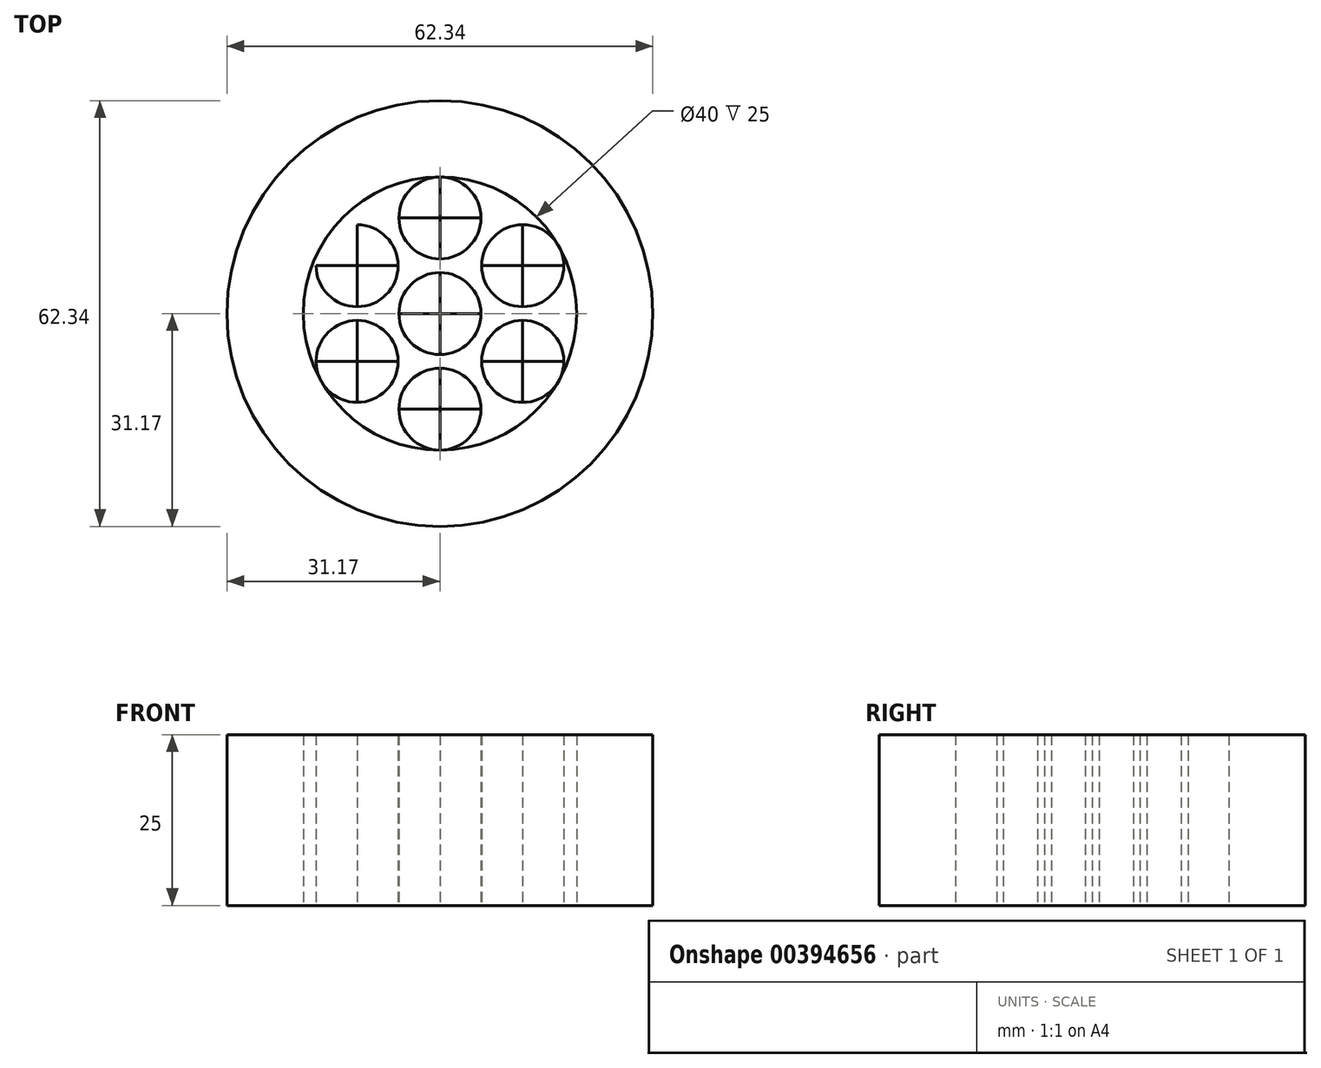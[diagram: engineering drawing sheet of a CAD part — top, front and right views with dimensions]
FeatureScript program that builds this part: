
annotation { "Feature Type Name" : "Feature", "Feature Type Description" : "" }
export const myFeature = defineFeature(function(context is Context, id is Id, definition is map)
    precondition{}
    {
        {
            var Q0;
            Q0=qCreatedBy(makeId("Top.planeOp"),FACE);
            var sketch = newSketch(context, id + "F0", { "sketchPlane" : qUnion([Q0])});
            skCircle(sketch, "E0", {"center": v(0, 0) * mm, "radius": 20 * mm});
            skCircle(sketch, "E1", {"center": v(0, 14) * mm, "radius": 6 * mm});
            skCircle(sketch, "E2.1.0", {"center": v(-12.12, 7) * mm, "radius": 6 * mm});
            skCircle(sketch, "E2.2.0", {"center": v(-12.12, -7) * mm, "radius": 6 * mm});
            skCircle(sketch, "E3.1.3.0", {"center": v(0, -14) * mm, "radius": 6 * mm});
            skCircle(sketch, "E3.1.4.0", {"center": v(12.12, -7) * mm, "radius": 6 * mm});
            skCircle(sketch, "E3.1.5.0", {"center": v(12.12, 7) * mm, "radius": 6 * mm});
            skCircle(sketch, "E4", {"center": v(0, 0) * mm, "radius": 6 * mm});
            skLineSegment(sketch, "E5", {"start": v(-18.12, 7) * mm, "end": v(-6.12, 7) * mm});
            skLineSegment(sketch, "E6", {"start": v(-18.12, -7) * mm, "end": v(-6.12, -7) * mm});
            skLineSegment(sketch, "E7", {"start": v(12.12, -13) * mm, "end": v(12.12, 13) * mm});
            skLineSegment(sketch, "E8", {"start": v(-12.12, -13) * mm, "end": v(-12.12, 13) * mm});
            skLineSegment(sketch, "E9", {"start": v(0, 14) * mm, "end": v(0, 20) * mm});
            skLineSegment(sketch, "E10", {"start": v(0, 14) * mm, "end": v(0, 8) * mm});
            skLineSegment(sketch, "E11", {"start": v(0, 0) * mm, "end": v(-6, 0) * mm});
            skLineSegment(sketch, "E12", {"start": v(0, 0) * mm, "end": v(6, 0) * mm});
            skLineSegment(sketch, "E13", {"start": v(0, 14) * mm, "end": v(-6, 14) * mm});
            skLineSegment(sketch, "E14", {"start": v(0, 14) * mm, "end": v(6, 14) * mm});
            skLineSegment(sketch, "E15", {"start": v(0, -14) * mm, "end": v(-6, -14) * mm});
            skLineSegment(sketch, "E16", {"start": v(0, -14) * mm, "end": v(6, -14) * mm});
            skLineSegment(sketch, "E17.trimOffspring", {"start": v(6.12, -7) * mm, "end": v(18.12, -7) * mm});
            skLineSegment(sketch, "E18.trimOffspring", {"start": v(0, -8) * mm, "end": v(0, -20) * mm});
            skLineSegment(sketch, "E19.trimOffspring", {"start": v(6.12, 7) * mm, "end": v(18.12, 7) * mm});
            skLineSegment(sketch, "E20.trimOffspring", {"start": v(0, 6) * mm, "end": v(0, -6) * mm});
            skCircle(sketch, "E21", {"center": v(0, 0) * mm, "radius": 31.17 * mm});
            skSolve(sketch);
        }
        {
            var Q0;
            {var subQ0=sQuery(id+"F0.wireOp",EDGE,"E16");Q0=makeQuery(id+"F0.imprint","IMPRINT",FACE,{"disambiguationData":[TD([[makeQuery(id+"F0.imprint","IMPRINT",EDGE,{"derivedFrom":subQ0}),-1.0]])]});}
            var Q1;
            {var subQ0=sQuery(id+"F0.wireOp",EDGE,"E15");Q1=makeQuery(id+"F0.imprint","IMPRINT",FACE,{"disambiguationData":[TD([[makeQuery(id+"F0.imprint","IMPRINT",EDGE,{"derivedFrom":subQ0}),-1.0]])]});}
            var Q2;
            {var subQ0=sQuery(id+"F0.wireOp",EDGE,"E8");var subQ1=sQuery(id+"F0.wireOp",EDGE,"E2.1.0");var subQ2=makeQuery(id+"F0.imprint","INTERSECT",VERTEX,{"disambiguationData":[OD(0.0)],"derivedFrom":[subQ1,subQ0]});Q2=makeQuery(id+"F0.imprint","IMPRINT",FACE,{"disambiguationData":[TD([[makeQuery(id+"F0.imprint","IMPRINT",EDGE,{"disambiguationData":[TD([[subQ2,-1.0]])],"derivedFrom":subQ1}),1.0]])]});}
            var Q3;
            {var subQ0=sQuery(id+"F0.wireOp",EDGE,"E11");Q3=makeQuery(id+"F0.imprint","IMPRINT",FACE,{"disambiguationData":[TD([[makeQuery(id+"F0.imprint","IMPRINT",EDGE,{"derivedFrom":subQ0}),-1.0]])]});}
            var Q4;
            {var subQ0=sQuery(id+"F0.wireOp",EDGE,"E12");Q4=makeQuery(id+"F0.imprint","IMPRINT",FACE,{"disambiguationData":[TD([[makeQuery(id+"F0.imprint","IMPRINT",EDGE,{"derivedFrom":subQ0}),-1.0]])]});}
            var Q5;
            {var subQ0=sQuery(id+"F0.wireOp",EDGE,"E9");Q5=makeQuery(id+"F0.imprint","IMPRINT",FACE,{"disambiguationData":[TD([[makeQuery(id+"F0.imprint","IMPRINT",EDGE,{"derivedFrom":subQ0}),1.0]])]});}
            var Q6;
            {var subQ0=sQuery(id+"F0.wireOp",EDGE,"E10");Q6=makeQuery(id+"F0.imprint","IMPRINT",FACE,{"disambiguationData":[TD([[makeQuery(id+"F0.imprint","IMPRINT",EDGE,{"derivedFrom":subQ0}),1.0]])]});}
            var Q7;
            {var subQ0=sQuery(id+"F0.wireOp",EDGE,"E5");var subQ1=sQuery(id+"F0.wireOp",EDGE,"E2.1.0");var subQ2=makeQuery(id+"F0.imprint","INTERSECT",VERTEX,{"disambiguationData":[OD(1.0)],"derivedFrom":[subQ1,subQ0]});Q7=makeQuery(id+"F0.imprint","IMPRINT",FACE,{"disambiguationData":[TD([[makeQuery(id+"F0.imprint","IMPRINT",EDGE,{"disambiguationData":[TD([[subQ2,1.0]])],"derivedFrom":subQ1}),1.0]])]});}
            var Q8;
            {var subQ0=sQuery(id+"F0.wireOp",EDGE,"E6");var subQ1=sQuery(id+"F0.wireOp",EDGE,"E2.2.0");var subQ2=makeQuery(id+"F0.imprint","INTERSECT",VERTEX,{"disambiguationData":[OD(0.0)],"derivedFrom":[subQ1,subQ0]});Q8=makeQuery(id+"F0.imprint","IMPRINT",FACE,{"disambiguationData":[TD([[makeQuery(id+"F0.imprint","IMPRINT",EDGE,{"disambiguationData":[TD([[subQ2,1.0]])],"derivedFrom":subQ1}),1.0]])]});}
            var Q9;
            {var subQ0=sQuery(id+"F0.wireOp",EDGE,"E6");var subQ1=sQuery(id+"F0.wireOp",EDGE,"E2.2.0");var subQ2=makeQuery(id+"F0.imprint","INTERSECT",VERTEX,{"disambiguationData":[OD(1.0)],"derivedFrom":[subQ1,subQ0]});Q9=makeQuery(id+"F0.imprint","IMPRINT",FACE,{"disambiguationData":[TD([[makeQuery(id+"F0.imprint","IMPRINT",EDGE,{"disambiguationData":[TD([[subQ2,1.0]])],"derivedFrom":subQ1}),1.0]])]});}
            var Q10;
            {var subQ0=sQuery(id+"F0.wireOp",EDGE,"E19.trimOffspring");var subQ1=sQuery(id+"F0.wireOp",EDGE,"E3.1.5.0");var subQ2=makeQuery(id+"F0.imprint","INTERSECT",VERTEX,{"disambiguationData":[OD(1.0)],"derivedFrom":[subQ1,subQ0]});Q10=makeQuery(id+"F0.imprint","IMPRINT",FACE,{"disambiguationData":[TD([[makeQuery(id+"F0.imprint","IMPRINT",EDGE,{"disambiguationData":[TD([[subQ2,1.0]])],"derivedFrom":subQ1}),1.0]])]});}
            var Q11;
            {var subQ0=sQuery(id+"F0.wireOp",EDGE,"E17.trimOffspring");var subQ1=sQuery(id+"F0.wireOp",EDGE,"E3.1.4.0");var subQ2=makeQuery(id+"F0.imprint","INTERSECT",VERTEX,{"disambiguationData":[OD(0.0)],"derivedFrom":[subQ1,subQ0]});Q11=makeQuery(id+"F0.imprint","IMPRINT",FACE,{"disambiguationData":[TD([[makeQuery(id+"F0.imprint","IMPRINT",EDGE,{"disambiguationData":[TD([[subQ2,1.0]])],"derivedFrom":subQ1}),1.0]])]});}
            var Q12;
            {var subQ0=sQuery(id+"F0.wireOp",EDGE,"E7");var subQ1=sQuery(id+"F0.wireOp",EDGE,"E3.1.4.0");var subQ2=makeQuery(id+"F0.imprint","INTERSECT",VERTEX,{"disambiguationData":[OD(0.0)],"derivedFrom":[subQ1,subQ0]});Q12=makeQuery(id+"F0.imprint","IMPRINT",FACE,{"disambiguationData":[TD([[makeQuery(id+"F0.imprint","IMPRINT",EDGE,{"disambiguationData":[TD([[subQ2,-1.0]])],"derivedFrom":subQ1}),1.0]])]});}
            var Q13;
            {var subQ0=sQuery(id+"F0.wireOp",EDGE,"E7");var subQ1=sQuery(id+"F0.wireOp",EDGE,"E3.1.5.0");var subQ2=makeQuery(id+"F0.imprint","INTERSECT",VERTEX,{"disambiguationData":[OD(0.0)],"derivedFrom":[subQ1,subQ0]});Q13=makeQuery(id+"F0.imprint","IMPRINT",FACE,{"disambiguationData":[TD([[makeQuery(id+"F0.imprint","IMPRINT",EDGE,{"disambiguationData":[TD([[subQ2,-1.0]])],"derivedFrom":subQ1}),1.0]])]});}
            extrude(context, id + "F1", {"entities" : qUnion([Q0, Q1, Q2, Q3, Q4, Q5, Q6, Q7, Q8, Q9, Q10, Q11, Q12, Q13]), "depth" : 25 * mm});
        }
        {
            var Q0;
            {var subQ0=sQuery(id+"F0.wireOp",EDGE,"E5");var subQ1=sQuery(id+"F0.wireOp",EDGE,"E2.1.0");var subQ2=makeQuery(id+"F0.imprint","INTERSECT",VERTEX,{"disambiguationData":[OD(1.0)],"derivedFrom":[subQ1,subQ0]});Q0=makeQuery(id+"F0.imprint","IMPRINT",FACE,{"disambiguationData":[TD([[makeQuery(id+"F0.imprint","IMPRINT",EDGE,{"disambiguationData":[TD([[subQ2,-1.0]])],"derivedFrom":subQ1}),1.0]])]});}
            var Q1;
            {var subQ0=sQuery(id+"F0.wireOp",EDGE,"E5");var subQ1=sQuery(id+"F0.wireOp",EDGE,"E2.1.0");var subQ2=makeQuery(id+"F0.imprint","INTERSECT",VERTEX,{"disambiguationData":[OD(0.0)],"derivedFrom":[subQ1,subQ0]});Q1=makeQuery(id+"F0.imprint","IMPRINT",FACE,{"disambiguationData":[TD([[makeQuery(id+"F0.imprint","IMPRINT",EDGE,{"disambiguationData":[TD([[subQ2,-1.0]])],"derivedFrom":subQ1}),1.0]])]});}
            var Q2;
            {var subQ0=sQuery(id+"F0.wireOp",EDGE,"E9");Q2=makeQuery(id+"F0.imprint","IMPRINT",FACE,{"disambiguationData":[TD([[makeQuery(id+"F0.imprint","IMPRINT",EDGE,{"derivedFrom":subQ0}),-1.0]])]});}
            var Q3;
            {var subQ0=sQuery(id+"F0.wireOp",EDGE,"E10");Q3=makeQuery(id+"F0.imprint","IMPRINT",FACE,{"disambiguationData":[TD([[makeQuery(id+"F0.imprint","IMPRINT",EDGE,{"derivedFrom":subQ0}),-1.0]])]});}
            var Q4;
            {var subQ0=sQuery(id+"F0.wireOp",EDGE,"E12");Q4=makeQuery(id+"F0.imprint","IMPRINT",FACE,{"disambiguationData":[TD([[makeQuery(id+"F0.imprint","IMPRINT",EDGE,{"derivedFrom":subQ0}),1.0]])]});}
            var Q5;
            {var subQ0=sQuery(id+"F0.wireOp",EDGE,"E11");Q5=makeQuery(id+"F0.imprint","IMPRINT",FACE,{"disambiguationData":[TD([[makeQuery(id+"F0.imprint","IMPRINT",EDGE,{"derivedFrom":subQ0}),1.0]])]});}
            var Q6;
            {var subQ0=sQuery(id+"F0.wireOp",EDGE,"E19.trimOffspring");var subQ1=sQuery(id+"F0.wireOp",EDGE,"E3.1.5.0");var subQ2=makeQuery(id+"F0.imprint","INTERSECT",VERTEX,{"disambiguationData":[OD(1.0)],"derivedFrom":[subQ1,subQ0]});Q6=makeQuery(id+"F0.imprint","IMPRINT",FACE,{"disambiguationData":[TD([[makeQuery(id+"F0.imprint","IMPRINT",EDGE,{"disambiguationData":[TD([[subQ2,-1.0]])],"derivedFrom":subQ1}),1.0]])]});}
            var Q7;
            {var subQ0=sQuery(id+"F0.wireOp",EDGE,"E17.trimOffspring");var subQ1=sQuery(id+"F0.wireOp",EDGE,"E3.1.4.0");var subQ2=makeQuery(id+"F0.imprint","INTERSECT",VERTEX,{"disambiguationData":[OD(1.0)],"derivedFrom":[subQ1,subQ0]});Q7=makeQuery(id+"F0.imprint","IMPRINT",FACE,{"disambiguationData":[TD([[makeQuery(id+"F0.imprint","IMPRINT",EDGE,{"disambiguationData":[TD([[subQ2,-1.0]])],"derivedFrom":subQ1}),1.0]])]});}
            var Q8;
            {var subQ0=sQuery(id+"F0.wireOp",EDGE,"E7");var subQ1=sQuery(id+"F0.wireOp",EDGE,"E3.1.4.0");var subQ2=makeQuery(id+"F0.imprint","INTERSECT",VERTEX,{"disambiguationData":[OD(0.0)],"derivedFrom":[subQ1,subQ0]});Q8=makeQuery(id+"F0.imprint","IMPRINT",FACE,{"disambiguationData":[TD([[makeQuery(id+"F0.imprint","IMPRINT",EDGE,{"disambiguationData":[TD([[subQ2,1.0]])],"derivedFrom":subQ1}),1.0]])]});}
            var Q9;
            {var subQ0=sQuery(id+"F0.wireOp",EDGE,"E16");Q9=makeQuery(id+"F0.imprint","IMPRINT",FACE,{"disambiguationData":[TD([[makeQuery(id+"F0.imprint","IMPRINT",EDGE,{"derivedFrom":subQ0}),1.0]])]});}
            var Q10;
            {var subQ0=sQuery(id+"F0.wireOp",EDGE,"E15");Q10=makeQuery(id+"F0.imprint","IMPRINT",FACE,{"disambiguationData":[TD([[makeQuery(id+"F0.imprint","IMPRINT",EDGE,{"derivedFrom":subQ0}),1.0]])]});}
            var Q11;
            {var subQ0=sQuery(id+"F0.wireOp",EDGE,"E6");var subQ1=sQuery(id+"F0.wireOp",EDGE,"E2.2.0");var subQ2=makeQuery(id+"F0.imprint","INTERSECT",VERTEX,{"disambiguationData":[OD(1.0)],"derivedFrom":[subQ1,subQ0]});Q11=makeQuery(id+"F0.imprint","IMPRINT",FACE,{"disambiguationData":[TD([[makeQuery(id+"F0.imprint","IMPRINT",EDGE,{"disambiguationData":[TD([[subQ2,-1.0]])],"derivedFrom":subQ1}),1.0]])]});}
            var Q12;
            {var subQ0=sQuery(id+"F0.wireOp",EDGE,"E6");var subQ1=sQuery(id+"F0.wireOp",EDGE,"E2.2.0");var subQ2=makeQuery(id+"F0.imprint","INTERSECT",VERTEX,{"disambiguationData":[OD(0.0)],"derivedFrom":[subQ1,subQ0]});Q12=makeQuery(id+"F0.imprint","IMPRINT",FACE,{"disambiguationData":[TD([[makeQuery(id+"F0.imprint","IMPRINT",EDGE,{"disambiguationData":[TD([[subQ2,-1.0]])],"derivedFrom":subQ1}),1.0]])]});}
            var Q13;
            {var subQ0=sQuery(id+"F0.wireOp",EDGE,"E19.trimOffspring");var subQ1=sQuery(id+"F0.wireOp",EDGE,"E3.1.5.0");var subQ2=makeQuery(id+"F0.imprint","INTERSECT",VERTEX,{"disambiguationData":[OD(0.0)],"derivedFrom":[subQ1,subQ0]});Q13=makeQuery(id+"F0.imprint","IMPRINT",FACE,{"disambiguationData":[TD([[makeQuery(id+"F0.imprint","IMPRINT",EDGE,{"disambiguationData":[TD([[subQ2,-1.0]])],"derivedFrom":subQ1}),1.0]])]});}
            extrude(context, id + "F2", {"entities" : qUnion([Q0, Q1, Q2, Q3, Q4, Q5, Q6, Q7, Q8, Q9, Q10, Q11, Q12, Q13]), "depth" : 25 * mm});
        }
        {
            var Q0;
            Q0=makeQuery(id+"F0.imprint","IMPRINT",FACE,{"disambiguationData":[TD([[makeQuery(id+"F0.imprint","IMPRINT",EDGE,{"derivedFrom":sQuery(id+"F0.wireOp",EDGE,"E21")}),1.0]])]});
            extrude(context, id + "F3", {"entities" : qUnion([Q0]), "depth" : 25 * mm});
        }
    });
